# Revit family: Sanitary_Sanitary-Accessories_hansgrohe_27921XXX-WallStoris-Tumbler_NEW
name_source: partatom
category: Furniture
revit_build: Autodesk Revit 2018 (Build: 20170223_1515(x64)
units: mm (PartAtom-declared; Revit-internal decimal feet)

## family parameters
Always vertical = No
Cut with Voids When Loaded = No
OmniClass Number = 23.40.20.00
OmniClass Title = General Furniture and Specialties
Room Calculation Point = No
Shared = No
Work Plane-Based = Yes

## types (2) — shared parameters
Always visible = Yes
BIMobject category = Sanitary Accessories
Default Elevation = 1219.2 mm
Design country = Germany
EAN code = 4059625352816
Edition number = 1
GTIN code = https://4059625352816
IFC Classification = Sanitary Terminal
Installation instructions = https://www.hansgrohe.com
Manufacturer country = Germany
Manufacturer name = hansgrohe
Material main = Plastic
Product Guid = 0b5410a0-6bf6-44d8-b7b2-ce40a4bf54dd
Product SKU = 27921XXX
Product data url = https://www.bimobject.com
Product family = WallStoris
Product group = Tooth brush tumbler
Product name = 27921XXX WallStoris Tumbler
Product url = https://www.hansgrohe.com
QR code = https://www.bimobject.com
Technical description = https://www.hansgrohe.com

## per-type parameters (varying)
| type | Material 1 |
| 700 Matt White | Hansgrohe - WallStoris - 700 Matt White |
| 670 Matte Black | Hansgrohe - WallStoris - 670 Matte Black |

## geometry (parser evidence)
native form markers: Sweep x2
no freeform markers — native parametric forms only
